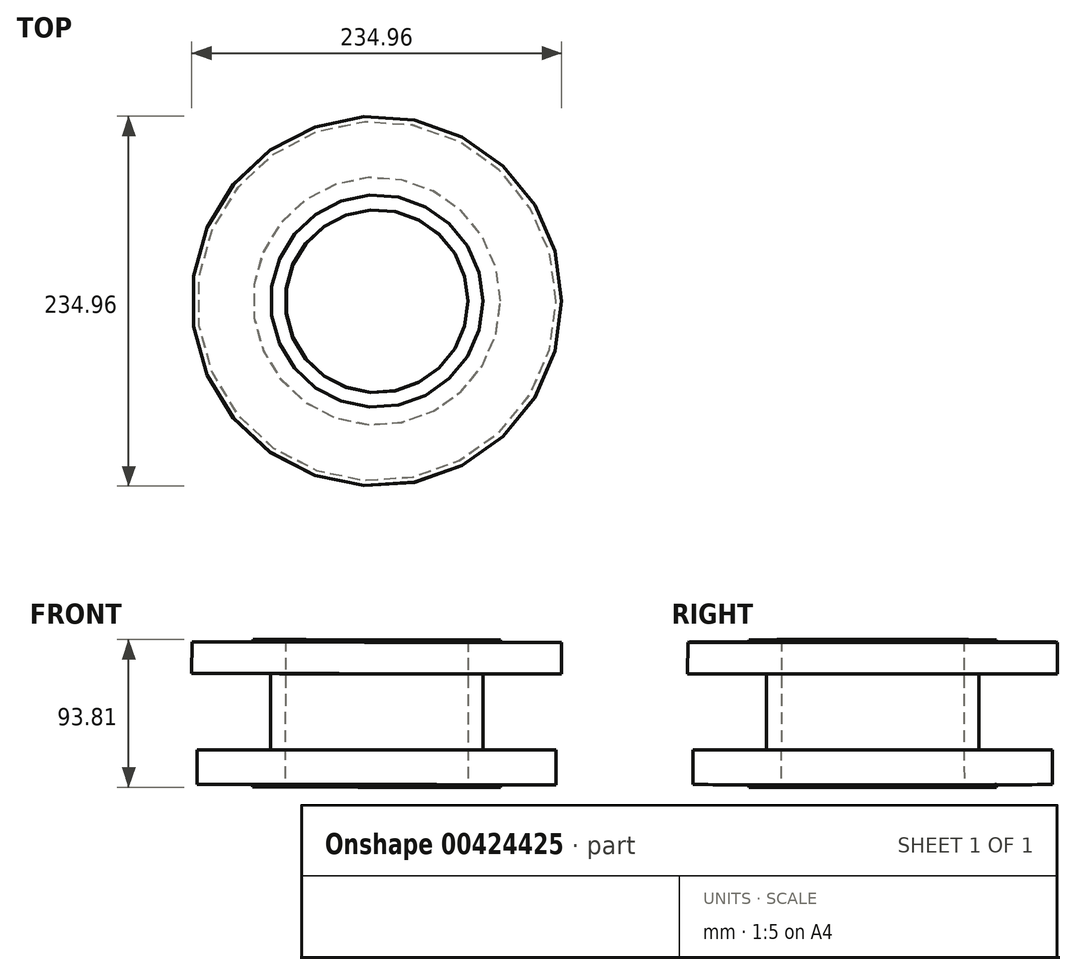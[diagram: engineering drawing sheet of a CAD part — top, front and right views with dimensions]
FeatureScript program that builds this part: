
annotation { "Feature Type Name" : "Feature", "Feature Type Description" : "" }
export const myFeature = defineFeature(function(context is Context, id is Id, definition is map)
    precondition{}
    {
        {
            var Q0;
            Q0=qCreatedBy(makeId("Front.planeOp"),FACE);
            var sketch = newSketch(context, id + "F0", { "sketchPlane" : qUnion([Q0])});
            skLineSegment(sketch, "E0", {"start": v(114, 23.6) * mm, "end": v(67.45, 23.6) * mm});
            skLineSegment(sketch, "E1", {"start": v(67.45, 23.6) * mm, "end": v(67.45, 72) * mm});
            skLineSegment(sketch, "E2", {"start": v(67.45, 72) * mm, "end": v(117.5, 72) * mm});
            skLineSegment(sketch, "E3", {"start": v(117.5, 72) * mm, "end": v(117.5, 92) * mm});
            skLineSegment(sketch, "E4", {"start": v(58.05, 93.6) * mm, "end": v(58.05, 0) * mm});
            skLineSegment(sketch, "E5", {"start": v(58.05, 0) * mm, "end": v(78.6, 0) * mm});
            skLineSegment(sketch, "E6", {"start": v(78.6, 0) * mm, "end": v(78.6, 1.6) * mm});
            skLineSegment(sketch, "E7", {"start": v(78.6, 1.6) * mm, "end": v(114, 1.6) * mm});
            skLineSegment(sketch, "E8", {"start": v(114, 1.6) * mm, "end": v(114, 23.6) * mm});
            skLineSegment(sketch, "E9", {"start": v(58.05, 93.6) * mm, "end": v(78.6, 93.6) * mm});
            skLineSegment(sketch, "E10", {"start": v(78.6, 93.6) * mm, "end": v(78.6, 92) * mm});
            skLineSegment(sketch, "E11", {"start": v(78.6, 92) * mm, "end": v(117.5, 92) * mm});
            skLineSegment(sketch, "E12", {"start": v(-0.08, 0.46) * mm, "end": v(0, 57.77) * mm, "construction": true});
            skSolve(sketch);
        }
        {
            var Q0;
            Q0 = qConstructionFilter(qBodyType(qCreatedBy(id + "F0" ,EDGE), BodyType.WIRE), ConstructionObject.NO);
            var Q1;
            Q1=sQuery(id+"F0.wireOp",EDGE,"E12");
            revolve(context, id + "F1", {"bodyType" : ToolBodyType.SURFACE, "surfaceEntities" : qUnion([Q0]), "axis" : qUnion([Q1]), "revolveType" : RevolveType.FULL});
        }
    });
